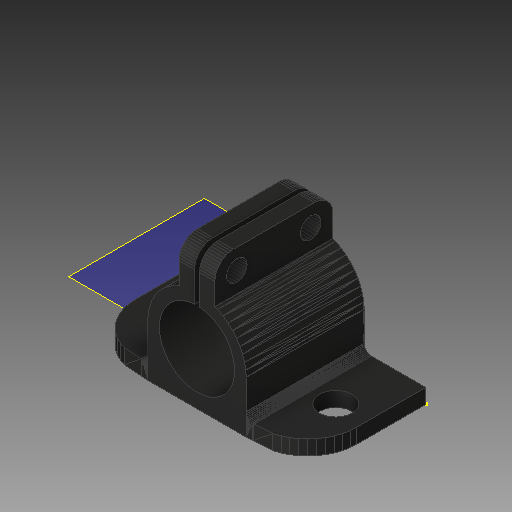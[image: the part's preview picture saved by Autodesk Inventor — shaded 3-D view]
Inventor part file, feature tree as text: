
AUTODESK INVENTOR PART (.ipt)
format: ipt  version: 2017 (Build 210142000, 142)  size: 676,864 bytes
history: native  units: mm
features: sketch x5, other x2, plane x2, extrude x2
ambient origin geometry x8: Origin, YZ Plane, XZ Plane, XY Plane, X Axis, Y Axis, Z Axis, Center Point
bodies: Solid1 (feature_tree)
feature tree (11):
  other  "12mm Rod Holder_fixed"
  plane  "Work Plane1"
  sketch  "Sketch2"  dims[d0=5.3mm d1=5.3mm]
  plane  "Work Plane2"
  sketch  "Sketch3"  dims[d2=10.0mm d3=0.0mm d4=12.2mm]
  other  "MeshFeature1"
  sketch  "Sketch4"  dims[d5=10.0mm d6=0.0mm]
  extrude  "Extrusion1"  Depth=5.3mm
  extrude  "Extrusion2"  Depth=10.0mm
  sketch  "Sketch5"
  sketch  "Sketch6"
